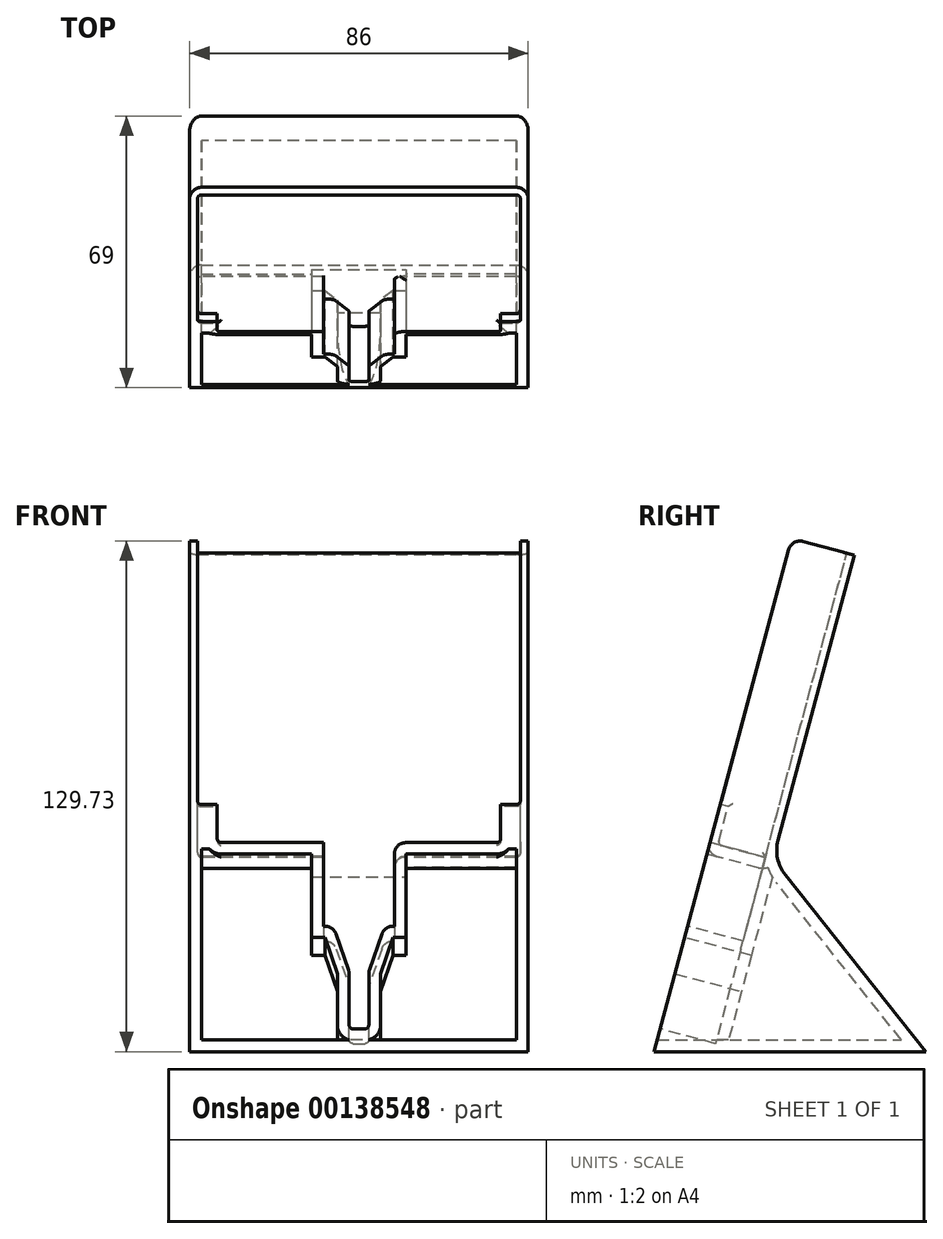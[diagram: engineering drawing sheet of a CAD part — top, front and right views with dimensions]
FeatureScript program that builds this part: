
annotation { "Feature Type Name" : "Feature", "Feature Type Description" : "" }
export const myFeature = defineFeature(function(context is Context, id is Id, definition is map)
    precondition{}
    {
        {
            var Q0;
            Q0=qCreatedBy(makeId("Right.planeOp"),FACE);
            var sketch = newSketch(context, id + "F0", { "sketchPlane" : qUnion([Q0])});
            skLineSegment(sketch, "E0", {"start": v(0, 0) * mm, "end": v(69, 0) * mm});
            skLineSegment(sketch, "E1", {"start": v(0, 0) * mm, "end": v(34.94, 130.4) * mm});
            skLineSegment(sketch, "E2", {"start": v(34.94, 130.4) * mm, "end": v(50.88, 126.13) * mm});
            skLineSegment(sketch, "E3", {"start": v(50.88, 126.13) * mm, "end": v(30.17, 48.86) * mm});
            skLineSegment(sketch, "E4", {"start": v(30.17, 48.86) * mm, "end": v(69, 0) * mm});
            skLineSegment(sketch, "E5", {"start": v(30.17, 48.86) * mm, "end": v(17.47, 52.26) * mm, "construction": true});
            skPoint(sketch, "E5.endSnap0", {"position": v(17.47, 65.2) * mm});
            skLineSegment(sketch, "E6", {"start": v(50.88, 126.13) * mm, "end": v(69, 193.74) * mm, "construction": true});
            skSolve(sketch);
        }
        {
            var Q0;
            Q0=qSketchRegion(id+"F0",true);
            extrude(context, id + "F1", {"entities" : qUnion([Q0]), "endBound" : BoundingType.SYMMETRIC, "depth" : 86 * mm});
        }
        {
            var Q0;
            Q0=makeQuery(id+"F1.opExtrude","SWEPT_FACE",FACE,{"disambiguationData":[OSD([sQuery(id+"F0.wireOp",EDGE,"E2")])]});
            var sketch = newSketch(context, id + "F2", { "sketchPlane" : qUnion([Q0])});
            skLineSegment(sketch, "E7.0", {"start": v(-41, 14.5) * mm, "end": v(-41, 2) * mm});
            skLineSegment(sketch, "E7.1", {"start": v(41, 14.5) * mm, "end": v(-41, 14.5) * mm});
            skLineSegment(sketch, "E7.2", {"start": v(41, 2) * mm, "end": v(41, 14.5) * mm});
            skLineSegment(sketch, "E7.3", {"start": v(-41, 2) * mm, "end": v(-36, 2) * mm});
            skLineSegment(sketch, "E8.0", {"start": v(36, 0) * mm, "end": v(-36, 0) * mm});
            skLineSegment(sketch, "E9", {"start": v(-36, 2) * mm, "end": v(-36, 0) * mm});
            skLineSegment(sketch, "E10.MirrorCS", {"start": v(36, 2) * mm, "end": v(36, 0) * mm});
            skPoint(sketch, "E11.orphan", {"position": v(-43, 0) * mm});
            skPoint(sketch, "E12.orphan", {"position": v(43, 0) * mm});
            skLineSegment(sketch, "E13.trimOffspring", {"start": v(36, 2) * mm, "end": v(41, 2) * mm});
            skSolve(sketch);
        }
        {
            var Q0;
            Q0=qSketchRegion(id+"F2",true);
            extrude(context, id + "F3", {"entities" : qUnion([Q0]), "operationType" : NewBodyOperationType.REMOVE, "oppositeDirection" : true, "depth" : 80 * mm});
        }
        {
            var Q0;
            Q0=makeQuery(id+"F1.opExtrude","SWEPT_FACE",FACE,{"disambiguationData":[OSD([sQuery(id+"F0.wireOp",EDGE,"E1")])]});
            var sketch = newSketch(context, id + "F4", { "sketchPlane" : qUnion([Q0])});
            skLineSegment(sketch, "E14.bottom", {"start": v(-36, 135) * mm, "end": v(-41, 135) * mm});
            skLineSegment(sketch, "E14.top", {"start": v(-36, 65) * mm, "end": v(-41, 65) * mm});
            skLineSegment(sketch, "E14.left", {"start": v(-36, 135) * mm, "end": v(-36, 65) * mm});
            skLineSegment(sketch, "E14.right", {"start": v(-41, 135) * mm, "end": v(-41, 65) * mm});
            skLineSegment(sketch, "E15.MirrorCS", {"start": v(36, 135) * mm, "end": v(41, 135) * mm});
            skLineSegment(sketch, "E16.MirrorCS", {"start": v(36, 65) * mm, "end": v(41, 65) * mm});
            skLineSegment(sketch, "E17.MirrorCS", {"start": v(36, 135) * mm, "end": v(36, 65) * mm});
            skLineSegment(sketch, "E18.MirrorCS", {"start": v(41, 135) * mm, "end": v(41, 65) * mm});
            skSolve(sketch);
        }
        {
            var Q0;
            Q0=qSketchRegion(id+"F4",true);
            extrude(context, id + "F5", {"entities" : qUnion([Q0]), "operationType" : NewBodyOperationType.REMOVE, "endBound" : BoundingType.UP_TO_NEXT, "oppositeDirection" : true, "depth" : 25 * mm});
        }
        {
            var Q0;
            Q0=makeQuery(id+"F1.opExtrude","SWEPT_FACE",FACE,{"disambiguationData":[OSD([sQuery(id+"F0.wireOp",EDGE,"E1")])]});
            var sketch = newSketch(context, id + "F6", { "sketchPlane" : qUnion([Q0])});
            skLineSegment(sketch, "E19.bottom", {"start": v(-9, 55) * mm, "end": v(9, 55) * mm});
            skLineSegment(sketch, "E19.top", {"start": v(-9, 33) * mm, "end": v(-6.5, 33) * mm});
            skLineSegment(sketch, "E19.left", {"start": v(-9, 55) * mm, "end": v(-9, 33) * mm});
            skLineSegment(sketch, "E19.right", {"start": v(9, 55) * mm, "end": v(9, 33) * mm});
            skLineSegment(sketch, "E20", {"start": v(-6.5, 33) * mm, "end": v(-2.5, 21) * mm});
            skLineSegment(sketch, "E21", {"start": v(-2.5, 21) * mm, "end": v(-2.5, 6) * mm});
            skLineSegment(sketch, "E22", {"start": v(-2.5, 6) * mm, "end": v(0, 6) * mm});
            skLineSegment(sketch, "E23.MirrorCS", {"start": v(6.5, 33) * mm, "end": v(2.5, 21) * mm});
            skLineSegment(sketch, "E24.MirrorCS", {"start": v(2.5, 21) * mm, "end": v(2.5, 6) * mm});
            skLineSegment(sketch, "E25.MirrorCS", {"start": v(2.5, 6) * mm, "end": v(0, 6) * mm});
            skLineSegment(sketch, "E26.trimOffspring", {"start": v(6.5, 33) * mm, "end": v(9, 33) * mm});
            skSolve(sketch);
        }
        {
            var Q0;
            Q0=qSketchRegion(id+"F6",true);
            var Q1;
            Q1=makeQuery(id+"F3.boolean.opBoolean","COPY",FACE,{"derivedFrom":makeQuery(id+"F3.opExtrude","SWEPT_FACE",FACE,{"disambiguationData":[OSD([sQuery(id+"F2.wireOp",EDGE,"E7.1")])]})});
            extrude(context, id + "F7", {"entities" : qUnion([Q0]), "operationType" : NewBodyOperationType.REMOVE, "endBound" : BoundingType.UP_TO_SURFACE, "oppositeDirection" : true, "endBoundEntityFace" : qUnion([Q1]), "depth" : 25 * mm});
        }
        {
            var Q0;
            Q0=makeQuery(id+"F3.boolean.opBoolean","COPY",EDGE,{"derivedFrom":makeQuery(id+"F3.opExtrude","SWEPT_EDGE",EDGE,{"disambiguationData":[OSD([sQuery(id+"F2.wireOp",EDGE,"E7.0"),sQuery(id+"F2.wireOp",EDGE,"E7.1")])]})});
            var Q1;
            Q1=makeQuery(id+"F3.boolean.opBoolean","COPY",EDGE,{"derivedFrom":makeQuery(id+"F3.opExtrude","CAP_EDGE",EDGE,{"disambiguationData":[OSD([sQuery(id+"F2.wireOp",EDGE,"E7.0")])],"isStart":false})});
            var Q2;
            {var subQ0=sQuery(id+"F2.wireOp",EDGE,"E7.1");var subQ1=sQuery(id+"F2.wireOp",EDGE,"E7.0");Q2=makeQuery(id+"F7.boolean.opBoolean","SPLIT",EDGE,{"disambiguationData":[TD([makeQuery(id+"F3.boolean.opBoolean","COPY",FACE,{"derivedFrom":makeQuery(id+"F3.opExtrude","SWEPT_FACE",FACE,{"disambiguationData":[OSD([subQ1])]})})])],"derivedFrom":makeQuery(id+"F3.boolean.opBoolean","COPY",EDGE,{"derivedFrom":makeQuery(id+"F3.opExtrude","CAP_EDGE",EDGE,{"disambiguationData":[OSD([subQ0])],"isStart":false})})});}
            var Q3;
            {var subQ0=sQuery(id+"F2.wireOp",EDGE,"E7.2");var subQ1=sQuery(id+"F2.wireOp",EDGE,"E7.1");Q3=makeQuery(id+"F7.boolean.opBoolean","SPLIT",EDGE,{"disambiguationData":[TD([makeQuery(id+"F3.boolean.opBoolean","COPY",FACE,{"derivedFrom":makeQuery(id+"F3.opExtrude","SWEPT_FACE",FACE,{"disambiguationData":[OSD([subQ0])]})})])],"derivedFrom":makeQuery(id+"F3.boolean.opBoolean","COPY",EDGE,{"derivedFrom":makeQuery(id+"F3.opExtrude","CAP_EDGE",EDGE,{"disambiguationData":[OSD([subQ1])],"isStart":false})})});}
            var Q4;
            Q4=makeQuery(id+"F7.boolean.opBoolean","COPY",EDGE,{"derivedFrom":makeQuery(id+"F7.opExtrude","TWEAK_EDGE",EDGE,{"derivedFrom":[makeQuery(id+"F3.boolean.opBoolean","COPY",FACE,{"derivedFrom":makeQuery(id+"F3.opExtrude","SWEPT_FACE",FACE,{"disambiguationData":[OSD([sQuery(id+"F2.wireOp",EDGE,"E7.1")])]})}),makeQuery(id+"F6.imprint","IMPRINT",EDGE,{"derivedFrom":sQuery(id+"F6.wireOp",EDGE,"E19.left")})]})});
            var Q5;
            Q5=makeQuery(id+"F7.boolean.opBoolean","COPY",EDGE,{"derivedFrom":makeQuery(id+"F7.opExtrude","TWEAK_EDGE",EDGE,{"derivedFrom":[makeQuery(id+"F3.boolean.opBoolean","COPY",FACE,{"derivedFrom":makeQuery(id+"F3.opExtrude","SWEPT_FACE",FACE,{"disambiguationData":[OSD([sQuery(id+"F2.wireOp",EDGE,"E7.1")])]})}),makeQuery(id+"F6.imprint","IMPRINT",EDGE,{"derivedFrom":sQuery(id+"F6.wireOp",EDGE,"E19.top")})]})});
            var Q6;
            Q6=makeQuery(id+"F7.boolean.opBoolean","COPY",EDGE,{"derivedFrom":makeQuery(id+"F7.opExtrude","TWEAK_EDGE",EDGE,{"derivedFrom":[makeQuery(id+"F3.boolean.opBoolean","COPY",FACE,{"derivedFrom":makeQuery(id+"F3.opExtrude","SWEPT_FACE",FACE,{"disambiguationData":[OSD([sQuery(id+"F2.wireOp",EDGE,"E7.1")])]})}),makeQuery(id+"F6.imprint","IMPRINT",EDGE,{"derivedFrom":sQuery(id+"F6.wireOp",EDGE,"E20")})]})});
            var Q7;
            Q7=makeQuery(id+"F7.boolean.opBoolean","COPY",EDGE,{"derivedFrom":makeQuery(id+"F7.opExtrude","TWEAK_EDGE",EDGE,{"derivedFrom":[makeQuery(id+"F3.boolean.opBoolean","COPY",FACE,{"derivedFrom":makeQuery(id+"F3.opExtrude","SWEPT_FACE",FACE,{"disambiguationData":[OSD([sQuery(id+"F2.wireOp",EDGE,"E7.1")])]})}),makeQuery(id+"F6.imprint","IMPRINT",EDGE,{"derivedFrom":sQuery(id+"F6.wireOp",EDGE,"E21")})]})});
            var Q8;
            Q8=makeQuery(id+"F7.boolean.opBoolean","COPY",EDGE,{"derivedFrom":makeQuery(id+"F7.opExtrude","TWEAK_EDGE",EDGE,{"derivedFrom":[makeQuery(id+"F3.boolean.opBoolean","COPY",FACE,{"derivedFrom":makeQuery(id+"F3.opExtrude","SWEPT_FACE",FACE,{"disambiguationData":[OSD([sQuery(id+"F2.wireOp",EDGE,"E7.1")])]})}),makeQuery(id+"F6.imprint","IMPRINT",EDGE,{"derivedFrom":sQuery(id+"F6.wireOp",EDGE,"E19.right")})]})});
            var Q9;
            Q9=makeQuery(id+"F7.boolean.opBoolean","COPY",EDGE,{"derivedFrom":makeQuery(id+"F7.opExtrude","TWEAK_EDGE",EDGE,{"derivedFrom":[makeQuery(id+"F3.boolean.opBoolean","COPY",FACE,{"derivedFrom":makeQuery(id+"F3.opExtrude","SWEPT_FACE",FACE,{"disambiguationData":[OSD([sQuery(id+"F2.wireOp",EDGE,"E7.1")])]})}),makeQuery(id+"F6.imprint","IMPRINT",EDGE,{"derivedFrom":sQuery(id+"F6.wireOp",EDGE,"E26.trimOffspring")})]})});
            var Q10;
            Q10=makeQuery(id+"F7.boolean.opBoolean","COPY",EDGE,{"derivedFrom":makeQuery(id+"F7.opExtrude","TWEAK_EDGE",EDGE,{"derivedFrom":[makeQuery(id+"F3.boolean.opBoolean","COPY",FACE,{"derivedFrom":makeQuery(id+"F3.opExtrude","SWEPT_FACE",FACE,{"disambiguationData":[OSD([sQuery(id+"F2.wireOp",EDGE,"E7.1")])]})}),makeQuery(id+"F6.imprint","IMPRINT",EDGE,{"derivedFrom":sQuery(id+"F6.wireOp",EDGE,"E23.MirrorCS")})]})});
            var Q11;
            Q11=makeQuery(id+"F7.boolean.opBoolean","COPY",EDGE,{"derivedFrom":makeQuery(id+"F7.opExtrude","TWEAK_EDGE",EDGE,{"derivedFrom":[makeQuery(id+"F3.boolean.opBoolean","COPY",FACE,{"derivedFrom":makeQuery(id+"F3.opExtrude","SWEPT_FACE",FACE,{"disambiguationData":[OSD([sQuery(id+"F2.wireOp",EDGE,"E7.1")])]})}),makeQuery(id+"F6.imprint","IMPRINT",EDGE,{"derivedFrom":sQuery(id+"F6.wireOp",EDGE,"E24.MirrorCS")})]})});
            var Q12;
            Q12=makeQuery(id+"F3.boolean.opBoolean","COPY",EDGE,{"derivedFrom":makeQuery(id+"F3.opExtrude","CAP_EDGE",EDGE,{"disambiguationData":[OSD([sQuery(id+"F2.wireOp",EDGE,"E10.MirrorCS")])],"isStart":false})});
            var Q13;
            Q13=makeQuery(id+"F3.boolean.opBoolean","COPY",EDGE,{"derivedFrom":makeQuery(id+"F3.opExtrude","CAP_EDGE",EDGE,{"disambiguationData":[OSD([sQuery(id+"F2.wireOp",EDGE,"E9")])],"isStart":false})});
            var Q14;
            Q14=makeQuery(id+"F3.boolean.opBoolean","COPY",EDGE,{"derivedFrom":makeQuery(id+"F3.opExtrude","SWEPT_EDGE",EDGE,{"disambiguationData":[OSD([sQuery(id+"F2.wireOp",EDGE,"E7.1"),sQuery(id+"F2.wireOp",EDGE,"E7.2")])]})});
            var Q15;
            Q15=makeQuery(id+"F3.boolean.opBoolean","COPY",EDGE,{"derivedFrom":makeQuery(id+"F3.opExtrude","CAP_EDGE",EDGE,{"disambiguationData":[OSD([sQuery(id+"F2.wireOp",EDGE,"E7.2")])],"isStart":false})});
            var Q16;
            Q16=makeQuery(id+"F5.boolean.opBoolean","COPY",EDGE,{"derivedFrom":makeQuery(id+"F5.opExtrude","SWEPT_EDGE",EDGE,{"disambiguationData":[OSD([sQuery(id+"F4.wireOp",EDGE,"E16.MirrorCS"),sQuery(id+"F4.wireOp",EDGE,"E18.MirrorCS")])]})});
            var Q17;
            Q17=makeQuery(id+"F3.boolean.opBoolean","COPY",EDGE,{"derivedFrom":makeQuery(id+"F3.opExtrude","CAP_EDGE",EDGE,{"disambiguationData":[OSD([sQuery(id+"F2.wireOp",EDGE,"E13.trimOffspring")])],"isStart":false})});
            var Q18;
            Q18=makeQuery(id+"F3.boolean.opBoolean","COPY",EDGE,{"derivedFrom":makeQuery(id+"F3.opExtrude","SWEPT_EDGE",EDGE,{"disambiguationData":[OSD([sQuery(id+"F2.wireOp",EDGE,"E7.2"),sQuery(id+"F2.wireOp",EDGE,"E13.trimOffspring")])]})});
            var Q19;
            Q19=makeQuery(id+"F3.boolean.opBoolean","COPY",EDGE,{"derivedFrom":makeQuery(id+"F3.opExtrude","CAP_EDGE",EDGE,{"disambiguationData":[OSD([sQuery(id+"F2.wireOp",EDGE,"E7.3")])],"isStart":false})});
            var Q20;
            Q20=makeQuery(id+"F5.boolean.opBoolean","COPY",EDGE,{"derivedFrom":makeQuery(id+"F5.opExtrude","SWEPT_EDGE",EDGE,{"disambiguationData":[OSD([sQuery(id+"F4.wireOp",EDGE,"E14.top"),sQuery(id+"F4.wireOp",EDGE,"E14.right")])]})});
            var Q21;
            Q21=makeQuery(id+"F3.boolean.opBoolean","COPY",EDGE,{"derivedFrom":makeQuery(id+"F3.opExtrude","SWEPT_EDGE",EDGE,{"disambiguationData":[OSD([sQuery(id+"F2.wireOp",EDGE,"E7.0"),sQuery(id+"F2.wireOp",EDGE,"E7.3")])]})});
            var Q22;
            Q22=makeQuery(id+"F5.boolean.opBoolean","COPY",EDGE,{"derivedFrom":makeQuery(id+"F5.opExtrude","SWEPT_EDGE",EDGE,{"disambiguationData":[OSD([sQuery(id+"F0.wireOp",EDGE,"E1"),sQuery(id+"F0.wireOp",EDGE,"E2"),sQuery(id+"F2.wireOp",EDGE,"E8.0"),sQuery(id+"F2.wireOp",EDGE,"E9"),sQuery(id+"F4.wireOp",EDGE,"E14.top"),sQuery(id+"F4.wireOp",EDGE,"E14.left")])]})});
            var Q23;
            Q23=makeQuery(id+"F5.boolean.opBoolean","COPY",EDGE,{"derivedFrom":makeQuery(id+"F5.opExtrude","SWEPT_EDGE",EDGE,{"disambiguationData":[OSD([sQuery(id+"F0.wireOp",EDGE,"E1"),sQuery(id+"F0.wireOp",EDGE,"E2"),sQuery(id+"F2.wireOp",EDGE,"E8.0"),sQuery(id+"F2.wireOp",EDGE,"E10.MirrorCS"),sQuery(id+"F4.wireOp",EDGE,"E16.MirrorCS"),sQuery(id+"F4.wireOp",EDGE,"E17.MirrorCS")])]})});
            var Q24;
            Q24=makeQuery(id+"F7.boolean.opBoolean","COPY",EDGE,{"derivedFrom":makeQuery(id+"F7.opExtrude","SWEPT_EDGE",EDGE,{"disambiguationData":[OSD([sQuery(id+"F6.wireOp",EDGE,"E21"),sQuery(id+"F6.wireOp",EDGE,"E22")])]})});
            var Q25;
            Q25=makeQuery(id+"F7.boolean.opBoolean","COPY",EDGE,{"derivedFrom":makeQuery(id+"F7.opExtrude","SWEPT_EDGE",EDGE,{"disambiguationData":[OSD([sQuery(id+"F6.wireOp",EDGE,"E24.MirrorCS"),sQuery(id+"F6.wireOp",EDGE,"E25.MirrorCS")])]})});
            fillet(context, id + "F8", {"entities" : qUnion([Q0, Q1, Q2, Q3, Q4, Q5, Q6, Q7, Q8, Q9, Q10, Q11, Q12, Q13, Q14, Q15, Q16, Q17, Q18, Q19, Q20, Q21, Q22, Q23, Q24, Q25]), "radius" : 1 * mm, "allowEdgeOverflow" : false});
        }
        {
            var Q0;
            Q0=makeQuery(id+"F7.boolean.opBoolean","COPY",EDGE,{"derivedFrom":makeQuery(id+"F7.opExtrude","CAP_EDGE",EDGE,{"disambiguationData":[OSD([sQuery(id+"F6.wireOp",EDGE,"E19.right")])],"isStart":true})});
            var Q1;
            Q1=makeQuery(id+"F7.boolean.opBoolean","COPY",EDGE,{"derivedFrom":makeQuery(id+"F7.opExtrude","CAP_EDGE",EDGE,{"disambiguationData":[OSD([sQuery(id+"F6.wireOp",EDGE,"E26.trimOffspring")])],"isStart":true})});
            var Q2;
            Q2=makeQuery(id+"F7.boolean.opBoolean","COPY",EDGE,{"derivedFrom":makeQuery(id+"F7.opExtrude","SWEPT_EDGE",EDGE,{"disambiguationData":[OSD([sQuery(id+"F6.wireOp",EDGE,"E23.MirrorCS"),sQuery(id+"F6.wireOp",EDGE,"E26.trimOffspring")])]})});
            var Q3;
            Q3=makeQuery(id+"F7.boolean.opBoolean","COPY",EDGE,{"derivedFrom":makeQuery(id+"F7.opExtrude","CAP_EDGE",EDGE,{"disambiguationData":[OSD([sQuery(id+"F6.wireOp",EDGE,"E23.MirrorCS")])],"isStart":true})});
            var Q4;
            Q4=makeQuery(id+"F7.boolean.opBoolean","COPY",EDGE,{"derivedFrom":makeQuery(id+"F7.opExtrude","SWEPT_EDGE",EDGE,{"disambiguationData":[OSD([sQuery(id+"F6.wireOp",EDGE,"E23.MirrorCS"),sQuery(id+"F6.wireOp",EDGE,"E24.MirrorCS")])]})});
            var Q5;
            Q5=makeQuery(id+"F7.boolean.opBoolean","COPY",EDGE,{"derivedFrom":makeQuery(id+"F7.opExtrude","CAP_EDGE",EDGE,{"disambiguationData":[OSD([sQuery(id+"F6.wireOp",EDGE,"E24.MirrorCS")])],"isStart":true})});
            var Q6;
            Q6=makeQuery(id+"F7.boolean.opBoolean","COPY",EDGE,{"derivedFrom":makeQuery(id+"F7.opExtrude","SWEPT_EDGE",EDGE,{"disambiguationData":[OSD([sQuery(id+"F6.wireOp",EDGE,"E20"),sQuery(id+"F6.wireOp",EDGE,"E21")])]})});
            var Q7;
            Q7=makeQuery(id+"F7.boolean.opBoolean","COPY",EDGE,{"derivedFrom":makeQuery(id+"F7.opExtrude","SWEPT_EDGE",EDGE,{"disambiguationData":[OSD([sQuery(id+"F6.wireOp",EDGE,"E19.top"),sQuery(id+"F6.wireOp",EDGE,"E20")])]})});
            var Q8;
            Q8=makeQuery(id+"F7.boolean.opBoolean","COPY",EDGE,{"derivedFrom":makeQuery(id+"F7.opExtrude","CAP_EDGE",EDGE,{"disambiguationData":[OSD([sQuery(id+"F6.wireOp",EDGE,"E19.left")])],"isStart":true})});
            var Q9;
            Q9=makeQuery(id+"F7.boolean.opBoolean","COPY",EDGE,{"derivedFrom":makeQuery(id+"F7.opExtrude","CAP_EDGE",EDGE,{"disambiguationData":[OSD([sQuery(id+"F6.wireOp",EDGE,"E19.top")])],"isStart":true})});
            var Q10;
            Q10=makeQuery(id+"F7.boolean.opBoolean","COPY",EDGE,{"derivedFrom":makeQuery(id+"F7.opExtrude","CAP_EDGE",EDGE,{"disambiguationData":[OSD([sQuery(id+"F6.wireOp",EDGE,"E21")])],"isStart":true})});
            var Q11;
            Q11=makeQuery(id+"F7.boolean.opBoolean","COPY",EDGE,{"derivedFrom":makeQuery(id+"F7.opExtrude","SWEPT_EDGE",EDGE,{"disambiguationData":[OSD([sQuery(id+"F2.wireOp",EDGE,"E8.0"),sQuery(id+"F6.wireOp",EDGE,"E19.bottom"),sQuery(id+"F6.wireOp",EDGE,"E19.left")])]})});
            var Q12;
            Q12=makeQuery(id+"F7.boolean.opBoolean","COPY",EDGE,{"derivedFrom":makeQuery(id+"F7.opExtrude","SWEPT_EDGE",EDGE,{"disambiguationData":[OSD([sQuery(id+"F2.wireOp",EDGE,"E8.0"),sQuery(id+"F6.wireOp",EDGE,"E19.bottom"),sQuery(id+"F6.wireOp",EDGE,"E19.right")])]})});
            var Q13;
            Q13=makeQuery(id+"F7.boolean.opBoolean","COPY",EDGE,{"derivedFrom":makeQuery(id+"F7.opExtrude","CAP_EDGE",EDGE,{"disambiguationData":[OSD([sQuery(id+"F6.wireOp",EDGE,"E20")])],"isStart":true})});
            fillet(context, id + "F9", {"entities" : qUnion([Q0, Q1, Q2, Q3, Q4, Q5, Q6, Q7, Q8, Q9, Q10, Q11, Q12, Q13]), "radius" : 3 * mm, "tangentPropagation" : true, "allowEdgeOverflow" : false});
        }
        {
            var Q0;
            Q0=makeQuery(id+"F1.opExtrude","SWEPT_EDGE",EDGE,{"disambiguationData":[OSD([sQuery(id+"F0.wireOp",EDGE,"E3"),sQuery(id+"F0.wireOp",EDGE,"E4")])]});
            fillet(context, id + "F10", {"entities" : qUnion([Q0]), "radius" : 10 * mm, "tangentPropagation" : true, "allowEdgeOverflow" : false});
        }
        {
            var Q0;
            {var subQ0=sQuery(id+"F0.wireOp",EDGE,"E2");var subQ1=sQuery(id+"F0.wireOp",EDGE,"E1");Q0=makeQuery(id+"F3.boolean.opBoolean","SPLIT",EDGE,{"disambiguationData":[TD([makeQuery(id+"F3.opExtrude","SWEPT_FACE",FACE,{"disambiguationData":[OSD([sQuery(id+"F2.wireOp",EDGE,"E10.MirrorCS")])]})])],"derivedFrom":makeQuery(id+"F1.opExtrude","SWEPT_EDGE",EDGE,{"disambiguationData":[OSD([subQ1,subQ0])]})});}
            var Q1;
            {var subQ0=sQuery(id+"F0.wireOp",EDGE,"E2");var subQ1=sQuery(id+"F0.wireOp",EDGE,"E1");Q1=makeQuery(id+"F3.boolean.opBoolean","SPLIT",EDGE,{"disambiguationData":[TD([makeQuery(id+"F3.opExtrude","SWEPT_FACE",FACE,{"disambiguationData":[OSD([sQuery(id+"F2.wireOp",EDGE,"E9")])]})])],"derivedFrom":makeQuery(id+"F1.opExtrude","SWEPT_EDGE",EDGE,{"disambiguationData":[OSD([subQ1,subQ0])]})});}
            var Q2;
            Q2=makeQuery(id+"F1.opExtrude","CAP_EDGE",EDGE,{"disambiguationData":[OSD([sQuery(id+"F0.wireOp",EDGE,"E3")])],"isStart":false});
            var Q3;
            Q3=makeQuery(id+"F1.opExtrude","CAP_EDGE",EDGE,{"disambiguationData":[OSD([sQuery(id+"F0.wireOp",EDGE,"E3")])],"isStart":true});
            fillet(context, id + "F11", {"entities" : qUnion([Q0, Q1, Q2, Q3]), "radius" : 3 * mm, "tangentPropagation" : true, "allowEdgeOverflow" : false});
        }
        {
            var Q0;
            Q0=makeQuery(id+"F1.opExtrude","SWEPT_FACE",FACE,{"disambiguationData":[OSD([sQuery(id+"F0.wireOp",EDGE,"E1")])]});
            shell(context, id + "F12", {"entities" : qUnion([Q0]), "thickness" : 3 * mm});
        }
    });
